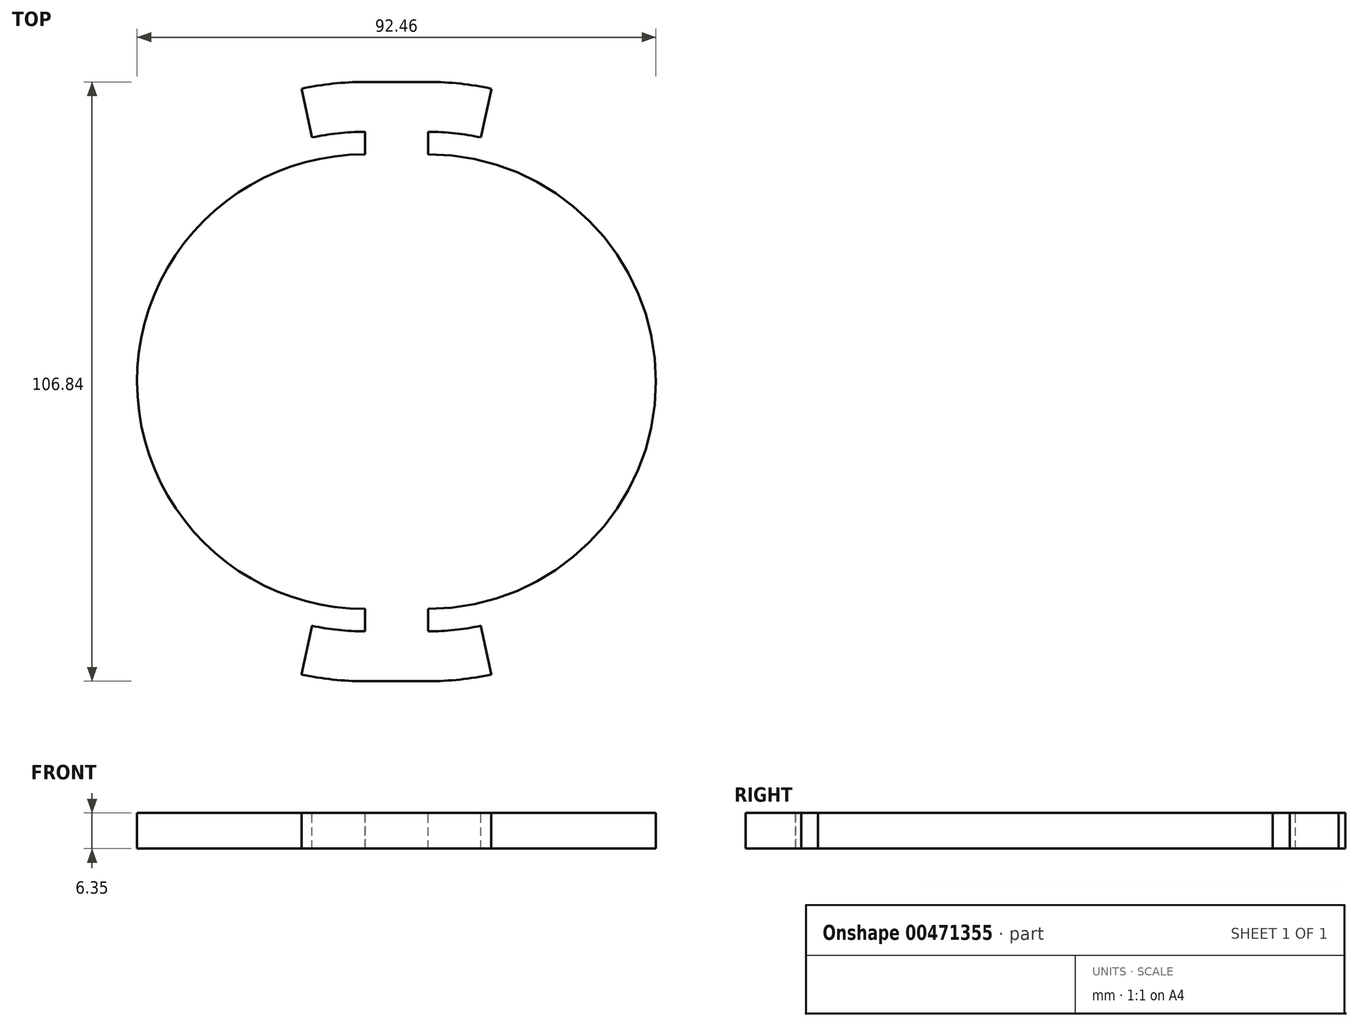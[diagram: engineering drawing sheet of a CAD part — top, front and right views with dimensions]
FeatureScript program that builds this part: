
annotation { "Feature Type Name" : "Feature", "Feature Type Description" : "" }
export const myFeature = defineFeature(function(context is Context, id is Id, definition is map)
    precondition{}
    {
        {
            var Q0;
            Q0=qCreatedBy(makeId("Top.planeOp"),FACE);
            var sketch = newSketch(context, id + "F0", { "sketchPlane" : qUnion([Q0])});
            skArc(sketch, "E0", {"start": v(-5.72, 44.45) * mm, "mid": v(-50.16, 0) * mm, "end": v(-5.71, -44.45) * mm, "construction": true});
            skArc(sketch, "E1", {"start": v(-5.72, 41.28) * mm, "mid": v(-47, 0) * mm, "end": v(-5.71, -41.28) * mm, "construction": true});
            skLineSegment(sketch, "E2.bottom", {"start": v(-88.64, 27.5) * mm, "end": v(-88.63, 27.5) * mm});
            skLineSegment(sketch, "E2.top", {"start": v(-88.64, 22.31) * mm, "end": v(-88.63, 22.31) * mm});
            skLineSegment(sketch, "E3", {"start": v(-5.72, 44.45) * mm, "end": v(-5.72, 41.28) * mm, "construction": true});
            skLineSegment(sketch, "E4.trimOffspring", {"start": v(-5.71, -41.28) * mm, "end": v(-5.71, -44.45) * mm, "construction": true});
            skArc(sketch, "E5.MirrorCS", {"start": v(5.72, 41.28) * mm, "mid": v(47, 0) * mm, "end": v(5.71, -41.28) * mm, "construction": true});
            skArc(sketch, "E6.0", {"start": v(-5.72, 40.51) * mm, "mid": v(-46.23, -0.06) * mm, "end": v(-5.6, -40.51) * mm});
            skArc(sketch, "E7.0", {"start": v(5.72, 40.51) * mm, "mid": v(46.23, 0) * mm, "end": v(5.72, -40.51) * mm});
            skLineSegment(sketch, "E8", {"start": v(-5.6, -40.51) * mm, "end": v(-5.52, -40.51) * mm, "construction": true});
            skLineSegment(sketch, "E9", {"start": v(-5.72, 40.51) * mm, "end": v(-5.52, 40.51) * mm});
            skPoint(sketch, "E10", {"position": v(-4.95, 40.51) * mm});
            skPoint(sketch, "E11", {"position": v(4.95, 40.51) * mm});
            skPoint(sketch, "E12", {"position": v(5.64, -40.51) * mm});
            skPoint(sketch, "E13", {"position": v(-5.52, -40.51) * mm});
            skLineSegment(sketch, "E14", {"start": v(-5.52, -40.51) * mm, "end": v(-5.52, -44.53) * mm, "construction": true});
            skLineSegment(sketch, "E15.MirrorCS", {"start": v(5.52, -40.51) * mm, "end": v(5.52, -44.53) * mm, "construction": true});
            skLineSegment(sketch, "E16", {"start": v(-5.52, -44.53) * mm, "end": v(5.52, -44.53) * mm, "construction": true});
            skLineSegment(sketch, "E17.0", {"start": v(-5.71, -53.42) * mm, "end": v(5.72, -53.42) * mm});
            skArc(sketch, "E18.0", {"start": v(-5.72, 53.42) * mm, "mid": v(-58.83, 5.63) * mm, "end": v(-16.91, -52.23) * mm, "construction": true});
            skArc(sketch, "E19.0", {"start": v(-5.72, 44.53) * mm, "mid": v(-50, 4.7) * mm, "end": v(-15.05, -43.54) * mm, "construction": true});
            skLineSegment(sketch, "E20", {"start": v(-5.52, -43.54) * mm, "end": v(-15.05, -43.54) * mm, "construction": true});
            skLineSegment(sketch, "E21", {"start": v(-15.05, -43.54) * mm, "end": v(-16.91, -52.23) * mm});
            skArc(sketch, "E22", {"start": v(-15.05, -43.54) * mm, "mid": v(-10.4, -44.28) * mm, "end": v(-5.72, -44.53) * mm});
            skArc(sketch, "E23", {"start": v(-16.91, -52.23) * mm, "mid": v(-11.34, -53.12) * mm, "end": v(-5.71, -53.42) * mm});
            skArc(sketch, "E24.MirrorCS", {"start": v(15.05, -43.54) * mm, "mid": v(10.4, -44.28) * mm, "end": v(5.72, -44.53) * mm});
            skLineSegment(sketch, "E25.MirrorCS", {"start": v(15.05, -43.54) * mm, "end": v(16.91, -52.23) * mm});
            skArc(sketch, "E26.MirrorCS", {"start": v(16.91, -52.23) * mm, "mid": v(11.34, -53.12) * mm, "end": v(5.71, -53.42) * mm});
            skLineSegment(sketch, "E27.MirrorCS", {"start": v(5.52, 40.51) * mm, "end": v(5.52, 40.51) * mm});
            skLineSegment(sketch, "E28", {"start": v(-5.52, 40.51) * mm, "end": v(5.52, 40.51) * mm, "construction": true});
            skLineSegment(sketch, "E29", {"start": v(5.52, 40.51) * mm, "end": v(5.72, 40.51) * mm});
            skLineSegment(sketch, "E30", {"start": v(5.52, -40.51) * mm, "end": v(5.64, -40.51) * mm, "construction": true});
            skLineSegment(sketch, "E31", {"start": v(-5.52, -40.51) * mm, "end": v(5.52, -40.51) * mm, "construction": true});
            skPoint(sketch, "E32.orphan", {"position": v(-5.64, -53.42) * mm});
            skPoint(sketch, "E33.orphan", {"position": v(5.64, -53.42) * mm});
            skArc(sketch, "E34", {"start": v(5.52, -44.53) * mm, "mid": v(5.58, -44.53) * mm, "end": v(5.64, -44.53) * mm, "construction": true});
            skArc(sketch, "E35.MirrorCS", {"start": v(-5.52, -44.53) * mm, "mid": v(-5.56, -44.53) * mm, "end": v(-5.6, -44.53) * mm, "construction": true});
            skLineSegment(sketch, "E36", {"start": v(5.64, -40.51) * mm, "end": v(5.64, -44.53) * mm});
            skArc(sketch, "E37", {"start": v(5.64, -44.53) * mm, "mid": v(5.68, -44.53) * mm, "end": v(5.72, -44.53) * mm});
            skLineSegment(sketch, "E38", {"start": v(5.64, -40.51) * mm, "end": v(5.72, -40.51) * mm});
            skLineSegment(sketch, "E39", {"start": v(-5.6, -40.51) * mm, "end": v(-5.6, -44.53) * mm});
            skArc(sketch, "E40", {"start": v(-5.6, -44.53) * mm, "mid": v(-5.66, -44.53) * mm, "end": v(-5.72, -44.53) * mm});
            skArc(sketch, "E41.MirrorCS", {"start": v(-5.68, 44.53) * mm, "mid": v(-5.7, 44.53) * mm, "end": v(-5.72, 44.53) * mm});
            skArc(sketch, "E42.MirrorCS", {"start": v(5.64, 44.53) * mm, "mid": v(5.68, 44.53) * mm, "end": v(5.72, 44.53) * mm});
            skArc(sketch, "E43.MirrorCS", {"start": v(-5.52, 44.53) * mm, "mid": v(-5.56, 44.53) * mm, "end": v(-5.6, 44.53) * mm, "construction": true});
            skArc(sketch, "E44.MirrorCS", {"start": v(5.52, 44.53) * mm, "mid": v(5.58, 44.53) * mm, "end": v(5.64, 44.53) * mm, "construction": true});
            skPoint(sketch, "E45.MirrorP", {"position": v(-5.64, 53.42) * mm});
            skPoint(sketch, "E46.MirrorP", {"position": v(5.64, 53.42) * mm});
            skArc(sketch, "E47.MirrorCS", {"start": v(15.05, 43.54) * mm, "mid": v(10.4, 44.28) * mm, "end": v(5.72, 44.53) * mm});
            skLineSegment(sketch, "E48.MirrorCS", {"start": v(-5.71, 41.28) * mm, "end": v(-5.71, 44.45) * mm, "construction": true});
            skLineSegment(sketch, "E49.MirrorCS", {"start": v(-5.52, 43.54) * mm, "end": v(-15.05, 43.54) * mm, "construction": true});
            skLineSegment(sketch, "E50.MirrorCS", {"start": v(-5.71, 53.42) * mm, "end": v(5.72, 53.42) * mm});
            skLineSegment(sketch, "E51.MirrorCS", {"start": v(15.05, 43.54) * mm, "end": v(16.91, 52.23) * mm});
            skArc(sketch, "E52.MirrorCS", {"start": v(16.91, 52.23) * mm, "mid": v(11.34, 53.12) * mm, "end": v(5.71, 53.42) * mm});
            skLineSegment(sketch, "E53.MirrorCS", {"start": v(-5.52, 44.53) * mm, "end": v(5.52, 44.53) * mm, "construction": true});
            skArc(sketch, "E54.MirrorCS", {"start": v(-15.05, 43.54) * mm, "mid": v(-10.4, 44.28) * mm, "end": v(-5.72, 44.53) * mm});
            skLineSegment(sketch, "E55.MirrorCS", {"start": v(-15.05, 43.54) * mm, "end": v(-16.91, 52.23) * mm});
            skArc(sketch, "E56.MirrorCS", {"start": v(-16.91, 52.23) * mm, "mid": v(-11.34, 53.12) * mm, "end": v(-5.71, 53.42) * mm});
            skLineSegment(sketch, "E57.MirrorCS", {"start": v(-5.6, 40.51) * mm, "end": v(-5.6, 44.45) * mm});
            skLineSegment(sketch, "E58.MirrorCS", {"start": v(5.64, 40.51) * mm, "end": v(5.64, 44.53) * mm});
            skPoint(sketch, "E59.newPointA", {"position": v(-5.6, 44.53) * mm});
            skPoint(sketch, "E59.newPointB", {"position": v(-5.6, 44.53) * mm});
            skArc(sketch, "E59.filletArc", {"start": v(-5.6, 44.45) * mm, "mid": v(-5.62, 44.5) * mm, "end": v(-5.68, 44.53) * mm});
            skSolve(sketch);
        }
        {
            var Q0;
            Q0 = qSketchRegion(id + "F0", true);
            extrude(context, id + "F1", {"entities" : qUnion([Q0]), "oppositeDirection" : true, "depth" : 6.35 * mm, "offsetDistance" : 25.4 * mm});
        }
        {
            var Q0;
            Q0=makeQuery(id+"F1.opExtrude","SWEPT_EDGE",EDGE,{"disambiguationData":[OSD([sQuery(id+"F0.wireOp",EDGE,"E21"),sQuery(id+"F0.wireOp",EDGE,"E23")])]});
            var Q1;
            Q1=makeQuery(id+"F1.opExtrude","SWEPT_EDGE",EDGE,{"disambiguationData":[OSD([sQuery(id+"F0.wireOp",EDGE,"E25.MirrorCS"),sQuery(id+"F0.wireOp",EDGE,"E26.MirrorCS")])]});
            var Q2;
            Q2=makeQuery(id+"F1.opExtrude","SWEPT_EDGE",EDGE,{"disambiguationData":[OSD([sQuery(id+"F0.wireOp",EDGE,"E24.MirrorCS"),sQuery(id+"F0.wireOp",EDGE,"E25.MirrorCS")])]});
            var Q3;
            Q3=makeQuery(id+"F1.opExtrude","SWEPT_EDGE",EDGE,{"disambiguationData":[OSD([sQuery(id+"F0.wireOp",EDGE,"E21"),sQuery(id+"F0.wireOp",EDGE,"E22")])]});
            var Q4;
            Q4=makeQuery(id+"F1.opExtrude","SWEPT_EDGE",EDGE,{"disambiguationData":[OSD([sQuery(id+"F0.wireOp",EDGE,"E15.MirrorCS"),sQuery(id+"F0.wireOp",EDGE,"E34")])]});
            var Q5;
            Q5=makeQuery(id+"F1.opExtrude","SWEPT_EDGE",EDGE,{"disambiguationData":[OSD([sQuery(id+"F0.wireOp",EDGE,"82a16c3e-2f24-40ca-8327-a302fd58a4510.MirrorCS"),sQuery(id+"F0.wireOp",EDGE,"c6884929-8ff0-40e0-9a69-bc25477c34b30.MirrorCS")])]});
            var Q6;
            Q6=makeQuery(id+"F1.opExtrude","SWEPT_EDGE",EDGE,{"disambiguationData":[OSD([sQuery(id+"F0.wireOp",EDGE,"c6884929-8ff0-40e0-9a69-bc25477c34b30.MirrorCS"),sQuery(id+"F0.wireOp",EDGE,"3f23fca3-ef5b-451b-a95f-de91029f33840.MirrorCS")])]});
            var Q7;
            Q7=makeQuery(id+"F1.opExtrude","SWEPT_EDGE",EDGE,{"disambiguationData":[OSD([sQuery(id+"F0.wireOp",EDGE,"16592d85-ebe4-4d53-ab6d-640fccc931960.MirrorCS"),sQuery(id+"F0.wireOp",EDGE,"fc5ee911-d5dc-465d-bda3-6774bf8384c50.MirrorCS")])]});
            var Q8;
            Q8=makeQuery(id+"F1.opExtrude","SWEPT_EDGE",EDGE,{"disambiguationData":[OSD([sQuery(id+"F0.wireOp",EDGE,"fc5ee911-d5dc-465d-bda3-6774bf8384c50.MirrorCS"),sQuery(id+"F0.wireOp",EDGE,"b7a96fb2-7da5-44ac-915b-e80d91595d8f0.MirrorCS")])]});
            var Q9;
            Q9=makeQuery(id+"F1.opExtrude","SWEPT_EDGE",EDGE,{"disambiguationData":[OSD([sQuery(id+"F0.wireOp",EDGE,"E9"),sQuery(id+"F0.wireOp",EDGE,"c26aad6d-71ae-482a-87fe-568186e7a25f0.MirrorCS")])]});
            var Q10;
            Q10=makeQuery(id+"F1.opExtrude","SWEPT_EDGE",EDGE,{"disambiguationData":[OSD([sQuery(id+"F0.wireOp",EDGE,"1eda140d-6f6e-46c3-951a-a65f4840df62"),sQuery(id+"F0.wireOp",EDGE,"E29")])]});
            var Q11;
            Q11=makeQuery(id+"F1.opExtrude","SWEPT_EDGE",EDGE,{"disambiguationData":[OSD([sQuery(id+"F0.wireOp",EDGE,"c26aad6d-71ae-482a-87fe-568186e7a25f0.MirrorCS"),sQuery(id+"F0.wireOp",EDGE,"62930b22-e17b-4466-b478-c37d8f6e4fa00.MirrorCS")])]});
            var Q12;
            Q12=makeQuery(id+"F1.opExtrude","SWEPT_EDGE",EDGE,{"disambiguationData":[OSD([sQuery(id+"F0.wireOp",EDGE,"1eda140d-6f6e-46c3-951a-a65f4840df62"),sQuery(id+"F0.wireOp",EDGE,"6517d1e0-12d1-4452-9c9c-78db9587899d0.MirrorCS")])]});
            var Q13;
            Q13=makeQuery(id+"F1.opExtrude","SWEPT_EDGE",EDGE,{"disambiguationData":[OSD([sQuery(id+"F0.wireOp",EDGE,"E14"),sQuery(id+"F0.wireOp",EDGE,"E35.MirrorCS")])]});
            var Q14;
            Q14=makeQuery(id+"F1.opExtrude","SWEPT_EDGE",EDGE,{"disambiguationData":[OSD([sQuery(id+"F0.wireOp",EDGE,"E15.MirrorCS"),sQuery(id+"F0.wireOp",EDGE,"E30")])]});
            var Q15;
            Q15=makeQuery(id+"F1.opExtrude","SWEPT_EDGE",EDGE,{"disambiguationData":[OSD([sQuery(id+"F0.wireOp",EDGE,"E8"),sQuery(id+"F0.wireOp",EDGE,"E14")])]});
            fillet(context, id + "F2", {"entities" : qUnion([Q0, Q1, Q2, Q3, Q4, Q5, Q6, Q7, Q8, Q9, Q10, Q11, Q12, Q13, Q14, Q15]), "radius" : 0.08 * mm, "tangentPropagation" : true, "allowEdgeOverflow" : false});
        }
    });
